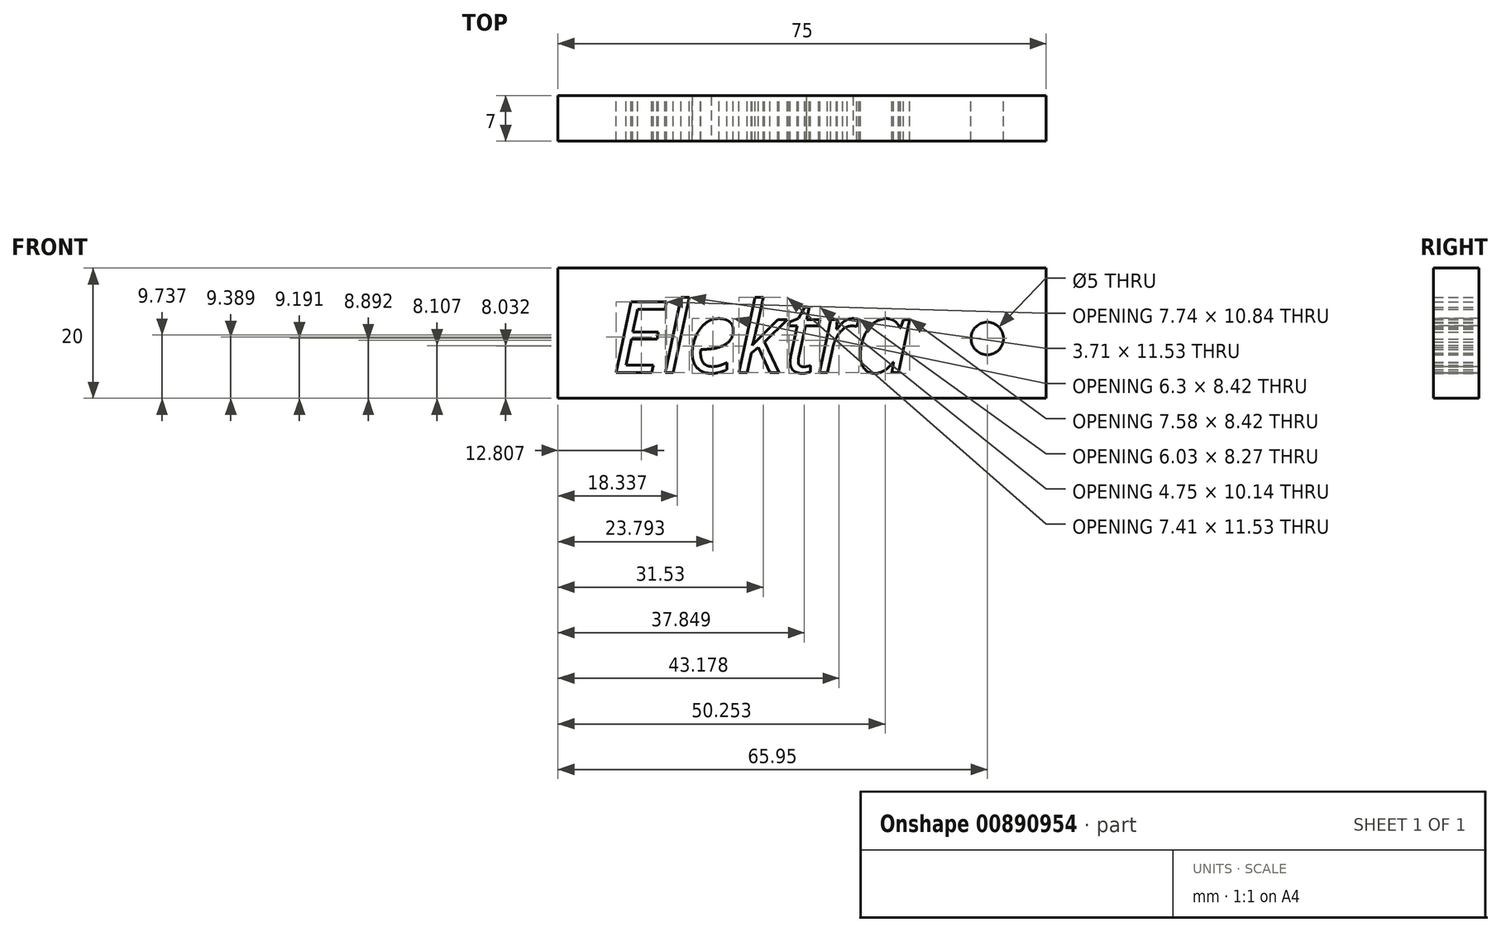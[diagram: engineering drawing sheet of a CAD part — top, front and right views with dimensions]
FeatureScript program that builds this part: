
annotation { "Feature Type Name" : "Feature", "Feature Type Description" : "" }
export const myFeature = defineFeature(function(context is Context, id is Id, definition is map)
    precondition{}
    {
        {
            var Q0;
            Q0=qCreatedBy(makeId("Front.planeOp"),FACE);
            var sketch = newSketch(context, id + "F0", { "sketchPlane" : qUnion([Q0])});
            skLineSegment(sketch, "E0.bottom", {"start": v(0, 0) * mm, "end": v(75, 0) * mm});
            skLineSegment(sketch, "E0.top", {"start": v(0, -20) * mm, "end": v(75, -20) * mm});
            skLineSegment(sketch, "E0.left", {"start": v(0, 0) * mm, "end": v(0, -20) * mm});
            skLineSegment(sketch, "E0.right", {"start": v(75, 0) * mm, "end": v(75, -20) * mm});
            skCircle(sketch, "E1", {"center": v(65.95, -10.8) * mm, "radius": 2.5 * mm});
            skText(sketch, "E2", { "text": "Elektra", "fontName": "OpenSans-Italic.ttf"});
            const initialGuessF0  = {"E2": [0.0083, -0.01603, 1, 0, 0.01093]};
            skSetInitialGuess(sketch, initialGuessF0);
            skSolve(sketch);
        }
        {
            var Q0;
            Q0 = qSketchRegion(id + "F0", true);
            extrude(context, id + "F1", {"entities" : qUnion([Q0]), "depth" : 7 * mm, "offsetDistance" : 25 * mm});
        }
    });
